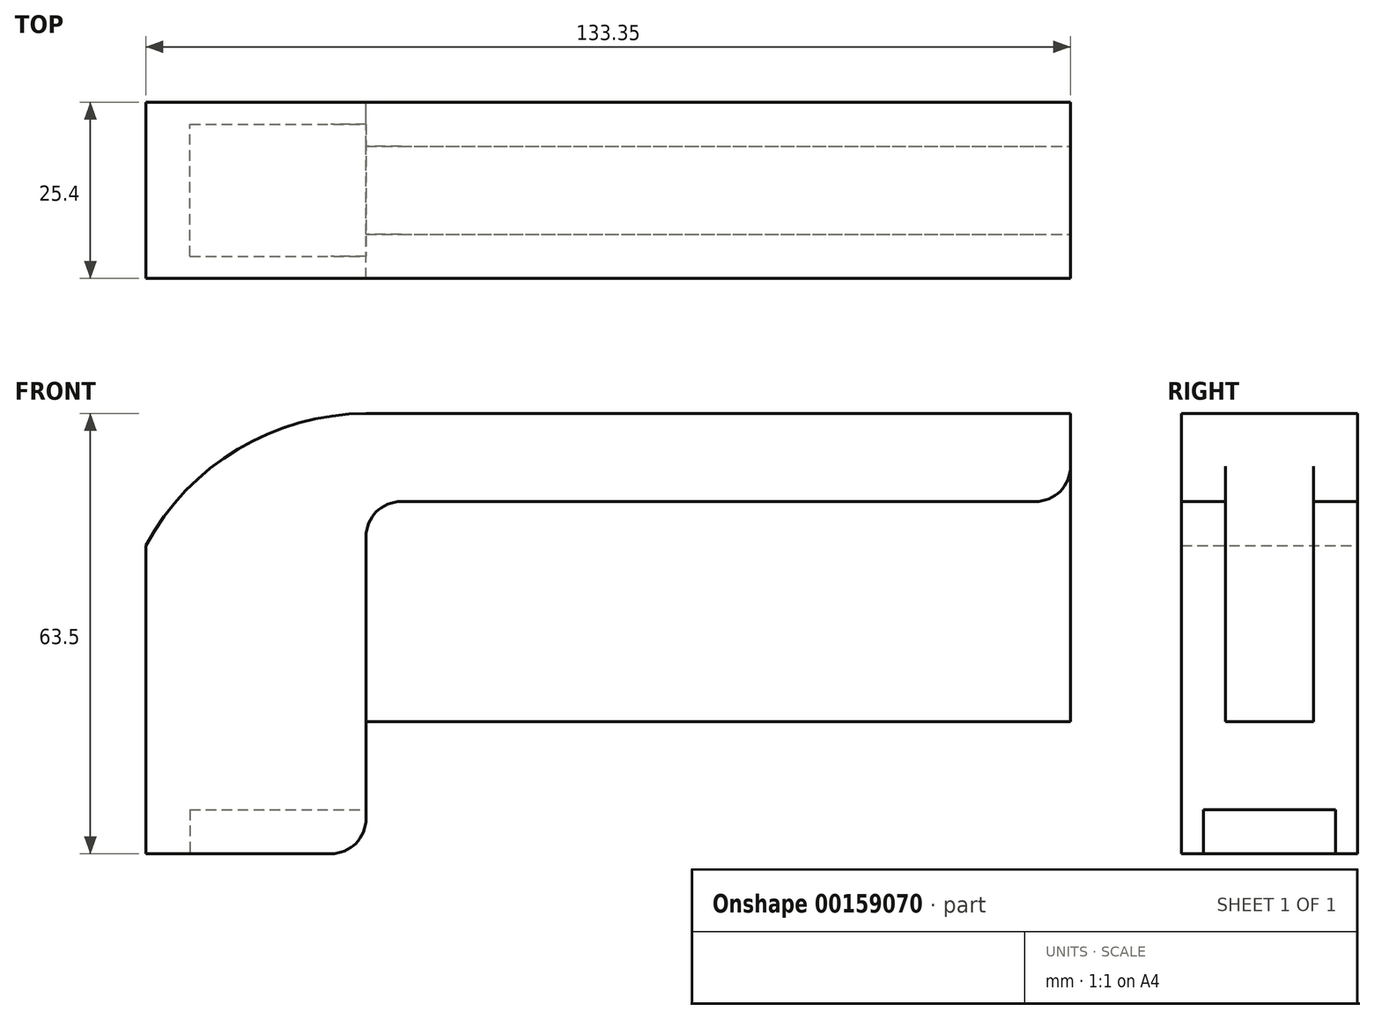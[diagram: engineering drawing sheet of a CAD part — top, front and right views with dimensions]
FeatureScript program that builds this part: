
annotation { "Feature Type Name" : "Feature", "Feature Type Description" : "" }
export const myFeature = defineFeature(function(context is Context, id is Id, definition is map)
    precondition{}
    {
        {
            var Q0;
            Q0=qCreatedBy(makeId("Front.planeOp"),FACE);
            var sketch = newSketch(context, id + "F0", { "sketchPlane" : qUnion([Q0])});
            skLineSegment(sketch, "E0.bottom", {"start": v(-82.55, 31.75) * mm, "end": v(82.55, 31.75) * mm});
            skLineSegment(sketch, "E0.top", {"start": v(-82.55, -31.75) * mm, "end": v(82.55, -31.75) * mm});
            skLineSegment(sketch, "E0.left", {"start": v(-82.55, 31.75) * mm, "end": v(-82.55, -31.75) * mm});
            skLineSegment(sketch, "E0.right", {"start": v(82.55, 31.75) * mm, "end": v(82.55, -31.75) * mm});
            skPoint(sketch, "E0.middle", {"position": v(0, 0) * mm});
            skLineSegment(sketch, "E1", {"start": v(-82.55, -31.75) * mm, "end": v(-50.8, -31.75) * mm});
            skLineSegment(sketch, "E2", {"start": v(-50.8, -31.75) * mm, "end": v(-50.8, -12.7) * mm});
            skLineSegment(sketch, "E3", {"start": v(-50.8, -12.7) * mm, "end": v(-50.8, 19.05) * mm});
            skLineSegment(sketch, "E4.bottom", {"start": v(-50.8, 19.05) * mm, "end": v(50.8, 19.05) * mm});
            skLineSegment(sketch, "E4.top", {"start": v(-50.8, -12.7) * mm, "end": v(50.8, -12.7) * mm});
            skLineSegment(sketch, "E4.left", {"start": v(-50.8, 19.05) * mm, "end": v(-50.8, -12.7) * mm});
            skLineSegment(sketch, "E4.right", {"start": v(50.8, 19.05) * mm, "end": v(50.8, -12.7) * mm});
            skLineSegment(sketch, "E5", {"start": v(-82.55, -31.75) * mm, "end": v(-82.55, 12.7) * mm});
            skPoint(sketch, "E6", {"position": v(82.55, 12.7) * mm});
            skLineSegment(sketch, "E7", {"start": v(-50.8, 19.05) * mm, "end": v(-50.8, 31.75) * mm});
            skLineSegment(sketch, "E8", {"start": v(50.8, 19.05) * mm, "end": v(50.8, 31.75) * mm});
            skArc(sketch, "E9", {"start": v(-50.8, 31.75) * mm, "mid": v(-69.3, 26.6) * mm, "end": v(-82.55, 12.7) * mm});
            skArc(sketch, "E10", {"start": v(82.55, 12.7) * mm, "mid": v(69.62, 27.14) * mm, "end": v(50.8, 31.75) * mm});
            skSolve(sketch);
        }
        {
            var Q0;
            Q0=makeQuery(id+"F0.imprint","IMPRINT",FACE,{"disambiguationData":[TD([[makeQuery(id+"F0.imprint","IMPRINT",EDGE,{"derivedFrom":sQuery(id+"F0.wireOp",EDGE,"E1")}),1.0]])]});
            var Q1;
            Q1=makeQuery(id+"F0.imprint","IMPRINT",FACE,{"disambiguationData":[TD([[makeQuery(id+"F0.imprint","IMPRINT",EDGE,{"derivedFrom":sQuery(id+"F0.wireOp",EDGE,"E4.bottom")}),1.0]])]});
            var Q2;
            {var subQ5=sQuery(id+"F0.wireOp",EDGE,"E0.top");Q2=makeQuery(id+"F0.imprint","IMPRINT",FACE,{"disambiguationData":[TD([[makeQuery(id+"F0.imprint","IMPRINT",EDGE,{"derivedFrom":subQ5}),1.0]])]});}
            extrude(context, id + "F1", {"entities" : qUnion([Q0, Q1, Q2]), "endBound" : BoundingType.SYMMETRIC, "depth" : 25.4 * mm});
        }
        {
            var Q0;
            Q0=makeQuery(id+"F0.imprint","IMPRINT",FACE,{"disambiguationData":[TD([[makeQuery(id+"F0.imprint","IMPRINT",EDGE,{"derivedFrom":sQuery(id+"F0.wireOp",EDGE,"E4.bottom")}),-1.0]])]});
            extrude(context, id + "F2", {"entities" : qUnion([Q0]), "operationType" : NewBodyOperationType.ADD, "endBound" : BoundingType.SYMMETRIC, "depth" : 12.7 * mm});
        }
        {
            var Q0;
            Q0=makeQuery(id+"F1.opExtrude","SWEPT_FACE",FACE,{"disambiguationData":[OSD([sQuery(id+"F0.wireOp",EDGE,"E0.top"),sQuery(id+"F0.wireOp",EDGE,"E1")])]});
            var sketch = newSketch(context, id + "F3", { "sketchPlane" : qUnion([Q0])});
            skLineSegment(sketch, "E11.bottom", {"start": v(-76.2, 9.52) * mm, "end": v(76.2, 9.52) * mm});
            skLineSegment(sketch, "E11.top", {"start": v(-76.2, -9.52) * mm, "end": v(76.2, -9.52) * mm});
            skLineSegment(sketch, "E11.left", {"start": v(-76.2, 9.52) * mm, "end": v(-76.2, -9.52) * mm});
            skLineSegment(sketch, "E11.right", {"start": v(76.2, 9.52) * mm, "end": v(76.2, -9.52) * mm});
            skPoint(sketch, "E11.middle", {"position": v(0, 0) * mm});
            skSolve(sketch);
        }
        {
            var Q0;
            Q0=makeQuery(id+"F3.imprint","IMPRINT",FACE,{"disambiguationData":[TD([[makeQuery(id+"F3.imprint","IMPRINT",EDGE,{"derivedFrom":sQuery(id+"F3.wireOp",EDGE,"E11.bottom")}),-1.0]])]});
            extrude(context, id + "F4", {"entities" : qUnion([Q0]), "operationType" : NewBodyOperationType.REMOVE, "oppositeDirection" : true, "depth" : 6.35 * mm});
        }
        {
            var Q0;
            Q0=makeQuery(id+"F4.boolean.opBoolean","COPY",FACE,{"derivedFrom":makeQuery(id+"F4.opExtrude","CAP_FACE",FACE,{"disambiguationData":[OSD([sQuery(id+"F3.wireOp",EDGE,"E11.bottom"),sQuery(id+"F3.wireOp",EDGE,"E11.top"),sQuery(id+"F3.wireOp",EDGE,"E11.left"),sQuery(id+"F3.wireOp",EDGE,"E11.right")])],"isStart":false})});
            var sketch = newSketch(context, id + "F5", { "sketchPlane" : qUnion([Q0])});
            skLineSegment(sketch, "E12.bottom", {"start": v(-38.1, 9.52) * mm, "end": v(38.1, 9.52) * mm});
            skLineSegment(sketch, "E12.top", {"start": v(-38.1, -9.52) * mm, "end": v(38.1, -9.52) * mm});
            skLineSegment(sketch, "E12.left", {"start": v(-38.1, 9.52) * mm, "end": v(-38.1, -9.52) * mm});
            skLineSegment(sketch, "E12.right", {"start": v(38.1, 9.52) * mm, "end": v(38.1, -9.52) * mm});
            skPoint(sketch, "E12.middle", {"position": v(0, 0) * mm});
            skSolve(sketch);
        }
        {
            var Q0;
            Q0=makeQuery(id+"F5.imprint","IMPRINT",FACE,{"disambiguationData":[TD([[makeQuery(id+"F5.imprint","IMPRINT",EDGE,{"derivedFrom":sQuery(id+"F5.wireOp",EDGE,"E12.bottom")}),-1.0]])]});
            extrude(context, id + "F6", {"entities" : qUnion([Q0]), "operationType" : NewBodyOperationType.REMOVE, "oppositeDirection" : true, "depth" : 10.16 * mm});
        }
        {
            var Q0;
            Q0=makeQuery(id+"F6.boolean.opBoolean","COPY",EDGE,{"derivedFrom":makeQuery(id+"F6.opExtrude","SWEPT_EDGE",EDGE,{"disambiguationData":[OSD([sQuery(id+"F3.wireOp",EDGE,"E11.bottom"),sQuery(id+"F5.wireOp",EDGE,"E12.bottom"),sQuery(id+"F5.wireOp",EDGE,"E12.left")])]})});
            var Q1;
            Q1=makeQuery(id+"F6.boolean.opBoolean","COPY",EDGE,{"derivedFrom":makeQuery(id+"F6.opExtrude","SWEPT_EDGE",EDGE,{"disambiguationData":[OSD([sQuery(id+"F3.wireOp",EDGE,"E11.bottom"),sQuery(id+"F5.wireOp",EDGE,"E12.bottom"),sQuery(id+"F5.wireOp",EDGE,"E12.right")])]})});
            var Q2;
            Q2=makeQuery(id+"F6.boolean.opBoolean","COPY",EDGE,{"derivedFrom":makeQuery(id+"F6.opExtrude","SWEPT_EDGE",EDGE,{"disambiguationData":[OSD([sQuery(id+"F3.wireOp",EDGE,"E11.top"),sQuery(id+"F5.wireOp",EDGE,"E12.top"),sQuery(id+"F5.wireOp",EDGE,"E12.right")])]})});
            var Q3;
            Q3=makeQuery(id+"F6.boolean.opBoolean","COPY",EDGE,{"derivedFrom":makeQuery(id+"F6.opExtrude","SWEPT_EDGE",EDGE,{"disambiguationData":[OSD([sQuery(id+"F3.wireOp",EDGE,"E11.top"),sQuery(id+"F5.wireOp",EDGE,"E12.top"),sQuery(id+"F5.wireOp",EDGE,"E12.left")])]})});
            var Q4;
            {var subQ0=sQuery(id+"F0.wireOp",EDGE,"E4.right");var subQ1=sQuery(id+"F0.wireOp",EDGE,"E4.left");var subQ2=sQuery(id+"F0.wireOp",EDGE,"E4.top");var subQ3=sQuery(id+"F0.wireOp",EDGE,"E4.bottom");Q4=makeQuery(id+"F2.boolean.opBoolean","SPLIT",EDGE,{"disambiguationData":[TD([makeQuery(id+"F2.opExtrude","CAP_FACE",FACE,{"disambiguationData":[OSD([subQ3,subQ2,subQ1,subQ0])],"isStart":false})])],"derivedFrom":makeQuery(id+"F1.opExtrude","SWEPT_EDGE",EDGE,{"disambiguationData":[OSD([subQ3,subQ1,sQuery(id+"F0.wireOp",EDGE,"E7")])]})});}
            var Q5;
            {var subQ0=sQuery(id+"F0.wireOp",EDGE,"E4.right");var subQ1=sQuery(id+"F0.wireOp",EDGE,"E4.left");var subQ2=sQuery(id+"F0.wireOp",EDGE,"E4.top");var subQ3=sQuery(id+"F0.wireOp",EDGE,"E4.bottom");Q5=makeQuery(id+"F2.boolean.opBoolean","SPLIT",EDGE,{"disambiguationData":[TD([makeQuery(id+"F2.opExtrude","CAP_FACE",FACE,{"disambiguationData":[OSD([subQ3,subQ2,subQ1,subQ0])],"isStart":false})])],"derivedFrom":makeQuery(id+"F1.opExtrude","SWEPT_EDGE",EDGE,{"disambiguationData":[OSD([sQuery(id+"F0.wireOp",EDGE,"E2"),subQ2,subQ1])]})});}
            var Q6;
            {var subQ0=sQuery(id+"F0.wireOp",EDGE,"E4.right");var subQ1=sQuery(id+"F0.wireOp",EDGE,"E4.left");var subQ2=sQuery(id+"F0.wireOp",EDGE,"E4.top");var subQ3=sQuery(id+"F0.wireOp",EDGE,"E4.bottom");Q6=makeQuery(id+"F2.boolean.opBoolean","SPLIT",EDGE,{"disambiguationData":[TD([makeQuery(id+"F2.opExtrude","CAP_FACE",FACE,{"disambiguationData":[OSD([subQ3,subQ2,subQ1,subQ0])],"isStart":false})])],"derivedFrom":makeQuery(id+"F1.opExtrude","SWEPT_EDGE",EDGE,{"disambiguationData":[OSD([subQ3,subQ0,sQuery(id+"F0.wireOp",EDGE,"E8")])]})});}
            var Q7;
            {var subQ0=sQuery(id+"F0.wireOp",EDGE,"E4.right");var subQ1=sQuery(id+"F0.wireOp",EDGE,"E4.left");var subQ2=sQuery(id+"F0.wireOp",EDGE,"E4.top");var subQ3=sQuery(id+"F0.wireOp",EDGE,"E4.bottom");Q7=makeQuery(id+"F2.boolean.opBoolean","SPLIT",EDGE,{"disambiguationData":[TD([makeQuery(id+"F2.opExtrude","CAP_FACE",FACE,{"disambiguationData":[OSD([subQ3,subQ2,subQ1,subQ0])],"isStart":false})])],"derivedFrom":makeQuery(id+"F1.opExtrude","SWEPT_EDGE",EDGE,{"disambiguationData":[OSD([subQ2,subQ0])]})});}
            var Q8;
            {var subQ0=sQuery(id+"F0.wireOp",EDGE,"E4.right");var subQ1=sQuery(id+"F0.wireOp",EDGE,"E4.left");var subQ2=sQuery(id+"F0.wireOp",EDGE,"E4.top");var subQ3=sQuery(id+"F0.wireOp",EDGE,"E4.bottom");Q8=makeQuery(id+"F2.boolean.opBoolean","SPLIT",EDGE,{"disambiguationData":[TD([makeQuery(id+"F2.opExtrude","CAP_FACE",FACE,{"disambiguationData":[OSD([subQ3,subQ2,subQ1,subQ0])],"isStart":true})])],"derivedFrom":makeQuery(id+"F1.opExtrude","SWEPT_EDGE",EDGE,{"disambiguationData":[OSD([subQ3,subQ0,sQuery(id+"F0.wireOp",EDGE,"E8")])]})});}
            var Q9;
            {var subQ0=sQuery(id+"F0.wireOp",EDGE,"E4.right");var subQ1=sQuery(id+"F0.wireOp",EDGE,"E4.left");var subQ2=sQuery(id+"F0.wireOp",EDGE,"E4.top");var subQ3=sQuery(id+"F0.wireOp",EDGE,"E4.bottom");Q9=makeQuery(id+"F2.boolean.opBoolean","SPLIT",EDGE,{"disambiguationData":[TD([makeQuery(id+"F2.opExtrude","CAP_FACE",FACE,{"disambiguationData":[OSD([subQ3,subQ2,subQ1,subQ0])],"isStart":true})])],"derivedFrom":makeQuery(id+"F1.opExtrude","SWEPT_EDGE",EDGE,{"disambiguationData":[OSD([subQ2,subQ0])]})});}
            var Q10;
            {var subQ0=sQuery(id+"F0.wireOp",EDGE,"E4.right");var subQ1=sQuery(id+"F0.wireOp",EDGE,"E4.left");var subQ2=sQuery(id+"F0.wireOp",EDGE,"E4.top");var subQ3=sQuery(id+"F0.wireOp",EDGE,"E4.bottom");Q10=makeQuery(id+"F2.boolean.opBoolean","SPLIT",EDGE,{"disambiguationData":[TD([makeQuery(id+"F2.opExtrude","CAP_FACE",FACE,{"disambiguationData":[OSD([subQ3,subQ2,subQ1,subQ0])],"isStart":true})])],"derivedFrom":makeQuery(id+"F1.opExtrude","SWEPT_EDGE",EDGE,{"disambiguationData":[OSD([subQ3,subQ1,sQuery(id+"F0.wireOp",EDGE,"E7")])]})});}
            var Q11;
            {var subQ0=sQuery(id+"F0.wireOp",EDGE,"E4.right");var subQ1=sQuery(id+"F0.wireOp",EDGE,"E4.left");var subQ2=sQuery(id+"F0.wireOp",EDGE,"E4.top");var subQ3=sQuery(id+"F0.wireOp",EDGE,"E4.bottom");Q11=makeQuery(id+"F2.boolean.opBoolean","SPLIT",EDGE,{"disambiguationData":[TD([makeQuery(id+"F2.opExtrude","CAP_FACE",FACE,{"disambiguationData":[OSD([subQ3,subQ2,subQ1,subQ0])],"isStart":true})])],"derivedFrom":makeQuery(id+"F1.opExtrude","SWEPT_EDGE",EDGE,{"disambiguationData":[OSD([sQuery(id+"F0.wireOp",EDGE,"E2"),subQ2,subQ1])]})});}
            fillet(context, id + "F7", {"entities" : qUnion([Q0, Q1, Q2, Q3, Q4, Q5, Q6, Q7, Q8, Q9, Q10, Q11]), "radius" : 5.08 * mm, "tangentPropagation" : true, "allowEdgeOverflow" : false});
        }
    });
